FCSTD DOCUMENT  (FreeCAD 0.20R29177 (Git))
Label: Assenbly
License: All rights reserved
LicenseURL: http://en.wikipedia.org/wiki/All_rights_reserved
objects: App::DocumentObjectGroup×3, PartDesign::CoordinateSystem×2, App::Link×2, App::FeaturePython×1, PartDesign::Body×1, App::Part×1, App::MeasureDistance×1
note: 3 computed .brp shape members not serialized (recipe doc carries the construction recipe); baked Part::Feature solids carry a one-line shape summary decoded from their .brp
EXTERNAL_REF file=CBEAM.FCStd obj=LCS_Origin
EXTERNAL_REF file=CBEAM.FCStd obj=Model

FEATURE [App::DocumentObjectGroup] Parts
FEATURE [PartDesign::CoordinateSystem] LCS_Origin
  AttacherType = Attacher::AttachEngine3D
  MapMode = 2
  Support = -> [X_Axis]
FEATURE [App::DocumentObjectGroup] Constraints
FEATURE [App::FeaturePython] Variables  # WARN: FeaturePython — macro-defined, semantics opaque (R4)
  Type = App::PropertyContainer
FEATURE [App::DocumentObjectGroup] Configurations
FEATURE [App::Link] CBEAM
  AttachedBy = #LCS_Origin
  AttachedTo = Parent Assembly#LCS_Origin
  LinkedObject = -> <external CBEAM.FCStd>#Model
  SolverId = Asm4EE
  expr: Placement = LCS_Origin.Placement * AttachmentOffset * CBEAM#LCS_Origin.Placement ^ -1
FEATURE [PartDesign::CoordinateSystem] LCS_2
  AttacherType = Attacher::AttachEngine3D
FEATURE [PartDesign::Body] Body
  Origin = -> Origin001
FEATURE [App::Link] Plate1
  AttachedBy = #LCS_Origin
  AttachedTo = Parent Assembly#LCS_Origin
  AttachmentOffset = pos=(-105.5,6.5,300) rot=(-0.57735,-0.57735,0.57735;4.18879rad)
  LinkPlacement = pos=(-105.5,6.5,300) rot=(-0.57735,-0.57735,0.57735;4.18879rad)
  Placement = pos=(-105.5,6.5,300) rot=(-0.57735,-0.57735,0.57735;4.18879rad)
  SolverId = Asm4EE
  expr: Placement = LCS_Origin.Placement * AttachmentOffset * Plate1#LCS_Origin.Placement ^ -1
FEATURE [App::Part] Model
  AssemblyType = Part::Link
  Group = -> [LCS_Origin,Constraints,Variables,Configurations,CBEAM,LCS_2,Plate1]
  Origin = -> Origin
  Type = Assembly
FEATURE [App::MeasureDistance] Distance  label="Distance: 40,00 mm"
  Distance = 40.0001
  P1 = (-76.316,-40,1000)
  P2 = (-76.2112,8.6e-15,1000)
